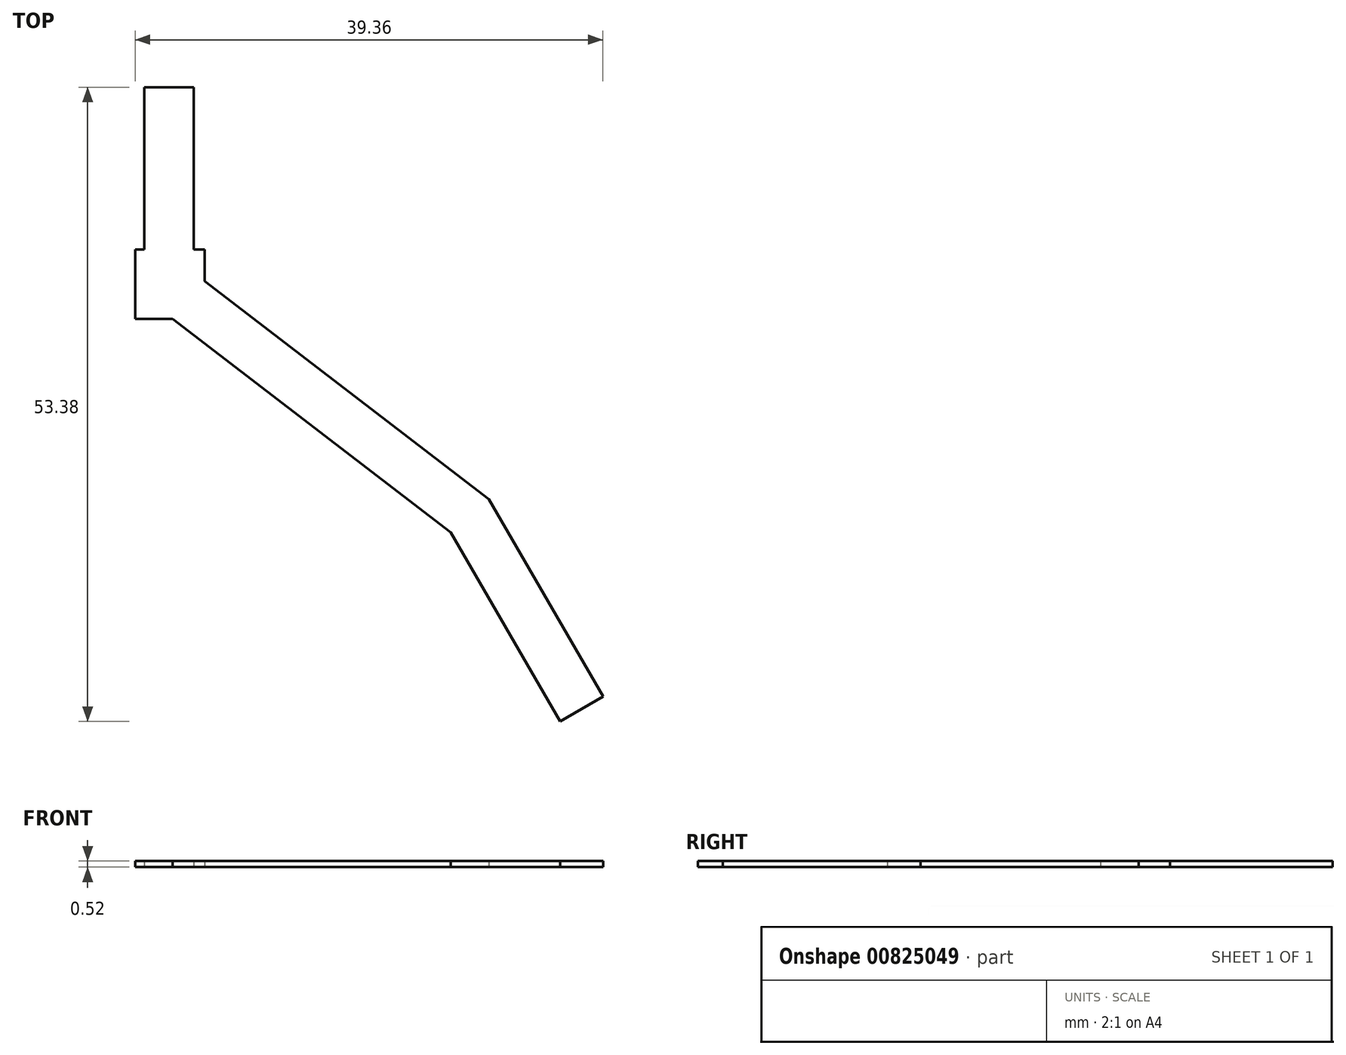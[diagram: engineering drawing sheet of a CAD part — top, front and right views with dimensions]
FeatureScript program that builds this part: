
annotation { "Feature Type Name" : "Feature", "Feature Type Description" : "" }
export const myFeature = defineFeature(function(context is Context, id is Id, definition is map)
    precondition{}
    {
        {
            var Q0;
            Q0=qCreatedBy(makeId("Top.planeOp"),FACE);
            var sketch = newSketch(context, id + "F0", { "sketchPlane" : qUnion([Q0])});
            skLineSegment(sketch, "E0", {"start": v(14.9, -7.22) * mm, "end": v(24.5, -23.85) * mm});
            skLineSegment(sketch, "E1", {"start": v(14.9, -7.22) * mm, "end": v(-9.02, 11.13) * mm});
            skLineSegment(sketch, "E2", {"start": v(11.7, -10.02) * mm, "end": v(20.9, -25.93) * mm});
            skLineSegment(sketch, "E3", {"start": v(20.9, -25.93) * mm, "end": v(24.5, -23.85) * mm});
            skLineSegment(sketch, "E4", {"start": v(-9.94, 13.78) * mm, "end": v(-9.94, 27.45) * mm});
            skLineSegment(sketch, "E5", {"start": v(11.7, -10.02) * mm, "end": v(-11.71, 7.94) * mm});
            skLineSegment(sketch, "E6", {"start": v(-14.1, 27.45) * mm, "end": v(-14.1, 13.78) * mm});
            skLineSegment(sketch, "E7.bottom", {"start": v(-14.86, 13.78) * mm, "end": v(-14.1, 13.78) * mm});
            skLineSegment(sketch, "E7.top", {"start": v(-14.86, 7.94) * mm, "end": v(-11.71, 7.94) * mm});
            skLineSegment(sketch, "E7.left", {"start": v(-14.86, 13.78) * mm, "end": v(-14.86, 7.94) * mm});
            skLineSegment(sketch, "E7.right", {"start": v(-9.02, 13.78) * mm, "end": v(-9.02, 11.13) * mm});
            skLineSegment(sketch, "E8.trimOffspring", {"start": v(-9.94, 13.78) * mm, "end": v(-9.02, 13.78) * mm});
            skLineSegment(sketch, "E9", {"start": v(-14.1, 27.45) * mm, "end": v(-9.94, 27.45) * mm});
            skSolve(sketch);
        }
        {
            var Q0;
            Q0 = qSketchRegion(id + "F0", true);
            extrude(context, id + "F1", {"entities" : qUnion([Q0]), "depth" : 0.52 * mm, "offsetDistance" : 25.4 * mm});
        }
    });
